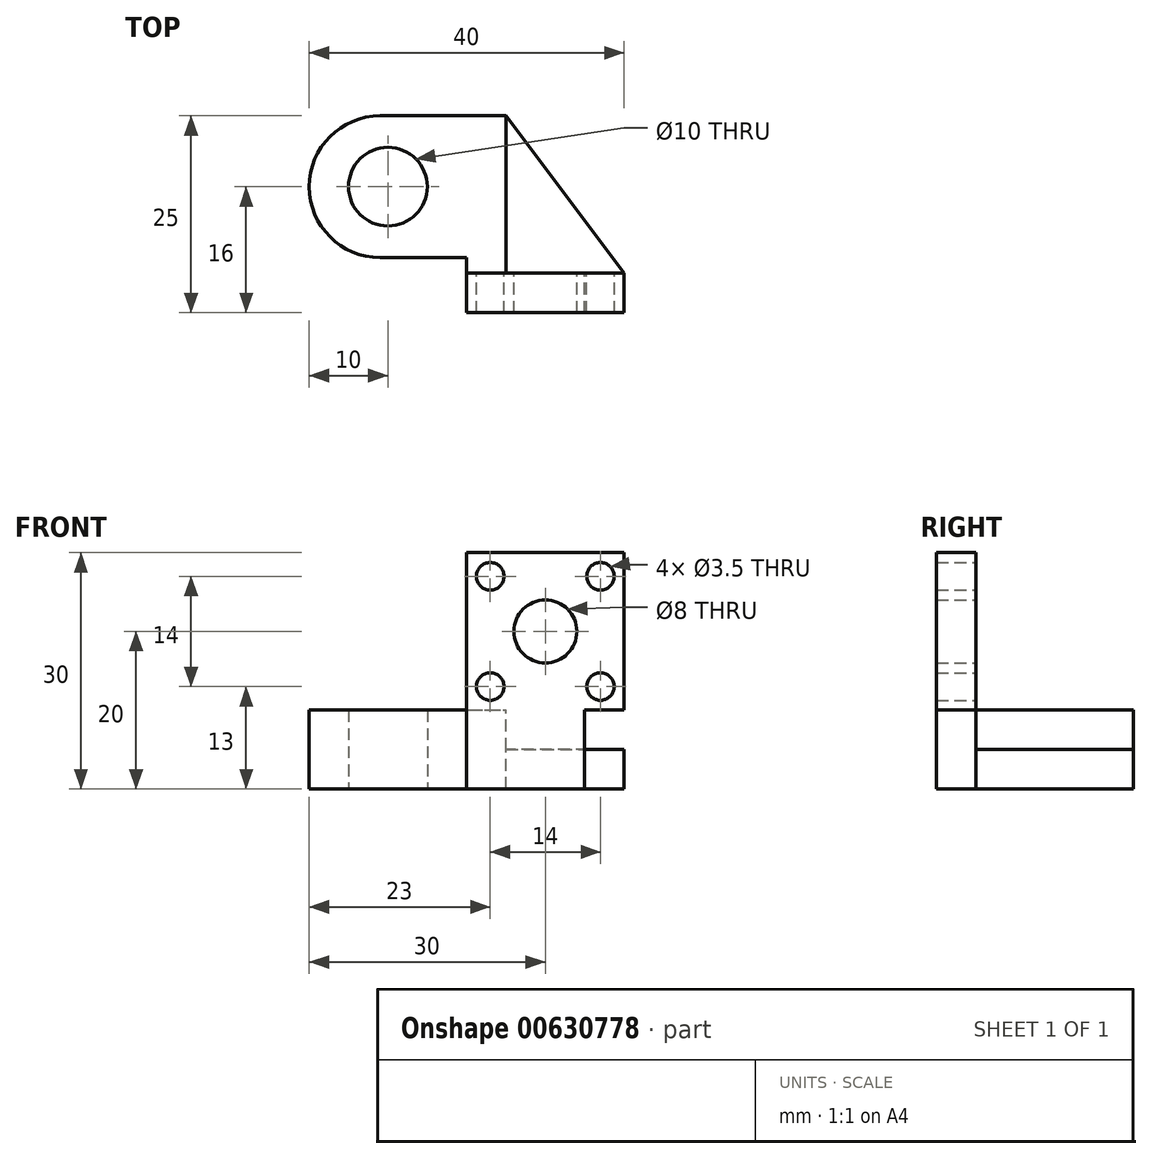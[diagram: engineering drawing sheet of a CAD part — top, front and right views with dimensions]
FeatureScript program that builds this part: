
annotation { "Feature Type Name" : "Feature", "Feature Type Description" : "" }
export const myFeature = defineFeature(function(context is Context, id is Id, definition is map)
    precondition{}
    {
        {
            var Q0;
            Q0=qCreatedBy(makeId("Front.planeOp"),FACE);
            var sketch = newSketch(context, id + "F0", { "sketchPlane" : qUnion([Q0])});
            skCircle(sketch, "E0", {"center": v(0, 0) * mm, "radius": 4 * mm});
            skLineSegment(sketch, "E1.bottom", {"start": v(10, 10) * mm, "end": v(-10, 10) * mm});
            skLineSegment(sketch, "E1.top", {"start": v(10, -20) * mm, "end": v(-10, -20) * mm});
            skLineSegment(sketch, "E1.left", {"start": v(10, 10) * mm, "end": v(10, -20) * mm});
            skLineSegment(sketch, "E1.right", {"start": v(-10, 10) * mm, "end": v(-10, -20) * mm});
            skCircle(sketch, "E2", {"center": v(-7, 7) * mm, "radius": 1.75 * mm});
            skCircle(sketch, "E3", {"center": v(7, 7) * mm, "radius": 1.75 * mm});
            skCircle(sketch, "E4", {"center": v(7, -7) * mm, "radius": 1.75 * mm});
            skCircle(sketch, "E5", {"center": v(-7, -7) * mm, "radius": 1.75 * mm});
            skLineSegment(sketch, "E6.bottom", {"start": v(10, -20) * mm, "end": v(5, -20) * mm});
            skLineSegment(sketch, "E6.top", {"start": v(10, -10) * mm, "end": v(5, -10) * mm});
            skLineSegment(sketch, "E6.left", {"start": v(10, -20) * mm, "end": v(10, -10) * mm});
            skLineSegment(sketch, "E6.right", {"start": v(5, -20) * mm, "end": v(5, -10) * mm});
            skLineSegment(sketch, "E7", {"start": v(0, 0) * mm, "end": v(0, 50.8) * mm, "construction": true});
            skLineSegment(sketch, "E8.MirrorCS", {"start": v(-5, -20) * mm, "end": v(-5, -10) * mm});
            skLineSegment(sketch, "E9.MirrorCS", {"start": v(-10, -10) * mm, "end": v(-5, -10) * mm});
            skSolve(sketch);
        }
        {
            var Q0;
            Q0=makeQuery(id+"F0.imprint","IMPRINT",FACE,{"disambiguationData":[TD([[makeQuery(id+"F0.imprint","IMPRINT",EDGE,{"derivedFrom":sQuery(id+"F0.wireOp",EDGE,"E0")}),-1.0]])]});
            var Q1;
            Q1=makeQuery(id+"F0.imprint","IMPRINT",FACE,{"disambiguationData":[TD([[makeQuery(id+"F0.imprint","IMPRINT",EDGE,{"derivedFrom":sQuery(id+"F0.wireOp",EDGE,"E6.bottom")}),-1.0]])]});
            extrude(context, id + "F1", {"entities" : qUnion([Q0, Q1]), "depth" : 5 * mm, "offsetDistance" : 25 * mm});
        }
        {
            var Q0;
            {var subQ3=sQuery(id+"F0.wireOp",EDGE,"E8.MirrorCS");Q0=makeQuery(id+"F0.imprint","IMPRINT",FACE,{"disambiguationData":[TD([[makeQuery(id+"F0.imprint","IMPRINT",EDGE,{"derivedFrom":subQ3}),1.0]])]});}
            extrude(context, id + "F2", {"entities" : qUnion([Q0]), "operationType" : NewBodyOperationType.ADD, "depth" : 5 * mm, "offsetDistance" : 25 * mm, "hasSecondDirection" : true, "secondDirectionOppositeDirection" : true, "secondDirectionDepth" : 20 * mm});
        }
        {
            var Q0;
            Q0=makeQuery(id+"F2.boolean.opBoolean","MERGE",FACE,{"derivedFrom":[makeQuery(id+"F1.opExtrude","SWEPT_FACE",FACE,{"disambiguationData":[OSD([sQuery(id+"F0.wireOp",EDGE,"E1.top")])]}),makeQuery(id+"F2.opExtrude","SWEPT_FACE",FACE,{"disambiguationData":[OSD([sQuery(id+"F0.wireOp",EDGE,"E6.bottom")])]})]});
            var sketch = newSketch(context, id + "F3", { "sketchPlane" : qUnion([Q0])});
            skLineSegment(sketch, "E10", {"start": v(0, 0) * mm, "end": v(0, 36.2) * mm, "construction": true});
            skLineSegment(sketch, "E11.MirrorCS", {"start": v(-10, -20) * mm, "end": v(-10, -2) * mm});
            skLineSegment(sketch, "E12.MirrorCS", {"start": v(-10, -2) * mm, "end": v(-21, -2) * mm});
            skCircle(sketch, "E13.MirrorC", {"center": v(-20, -11) * mm, "radius": 5 * mm});
            skArc(sketch, "E14.MirrorCS", {"start": v(-30, -11) * mm, "mid": v(-27.36, -4.64) * mm, "end": v(-21, -2) * mm});
            skArc(sketch, "E15.MirrorCS", {"start": v(-21, -20) * mm, "mid": v(-27.36, -17.36) * mm, "end": v(-30, -11) * mm});
            skLineSegment(sketch, "E16.MirrorCS", {"start": v(-10, -20) * mm, "end": v(-21, -20) * mm});
            skLineSegment(sketch, "E17.MirrorCS", {"start": v(-20, 8.06) * mm, "end": v(-20, -30.28) * mm, "construction": true});
            skLineSegment(sketch, "E18.MirrorCS", {"start": v(19.44, -11) * mm, "end": v(-30, -11) * mm, "construction": true});
            skSolve(sketch);
        }
        {
            var Q0;
            Q0=makeQuery(id+"F3.imprint","IMPRINT",FACE,{"disambiguationData":[TD([[makeQuery(id+"F3.imprint","IMPRINT",EDGE,{"derivedFrom":sQuery(id+"F3.wireOp",EDGE,"E11.MirrorCS")}),-1.0]])]});
            extrude(context, id + "F4", {"entities" : qUnion([Q0]), "operationType" : NewBodyOperationType.ADD, "oppositeDirection" : true, "depth" : 10 * mm, "offsetDistance" : 25 * mm});
        }
        {
            var Q0;
            Q0=makeQuery(id+"F4.boolean.opBoolean","MERGE",FACE,{"derivedFrom":[makeQuery(id+"F2.boolean.opBoolean","MERGE",FACE,{"derivedFrom":[makeQuery(id+"F1.opExtrude","SWEPT_FACE",FACE,{"disambiguationData":[OSD([sQuery(id+"F0.wireOp",EDGE,"E1.top")])]}),makeQuery(id+"F2.opExtrude","SWEPT_FACE",FACE,{"disambiguationData":[OSD([sQuery(id+"F0.wireOp",EDGE,"E6.bottom")])]})]}),makeQuery(id+"F4.opExtrude","CAP_FACE",FACE,{"disambiguationData":[OSD([sQuery(id+"F3.wireOp",EDGE,"ABPhrq3E-RsWc-z5md-EiWi-Qo4oXEG86XOk.bottom"),sQuery(id+"F3.wireOp",EDGE,"ABPhrq3E-RsWc-z5md-EiWi-Qo4oXEG86XOk.top"),sQuery(id+"F3.wireOp",EDGE,"ABPhrq3E-RsWc-z5md-EiWi-Qo4oXEG86XOk.left"),sQuery(id+"F3.wireOp",EDGE,"XPBqMR5t-pk4j-waNs-Rl70-sSKM0ePCXRSr"),sQuery(id+"F3.wireOp",EDGE,"753d2c3b-d90f-4cd3-bb09-2d7a23aacffc.filletArc"),sQuery(id+"F3.wireOp",EDGE,"1a6af256-a69d-40ec-95a1-83ec94e579a9.filletArc")])],"isStart":true})]});
            var sketch = newSketch(context, id + "F5", { "sketchPlane" : qUnion([Q0])});
            skLineSegment(sketch, "E19", {"start": v(-10, 0) * mm, "end": v(10, 0) * mm});
            skLineSegment(sketch, "E20", {"start": v(10, 0) * mm, "end": v(-5, -20) * mm});
            skLineSegment(sketch, "E21", {"start": v(-5, -20) * mm, "end": v(-10, 0) * mm});
            skSolve(sketch);
        }
        {
            var Q0;
            Q0=makeQuery(id+"F5.imprint","IMPRINT",FACE,{"disambiguationData":[TD([[makeQuery(id+"F5.imprint","IMPRINT",EDGE,{"derivedFrom":sQuery(id+"F5.wireOp",EDGE,"E19")}),1.0]])]});
            extrude(context, id + "F6", {"entities" : qUnion([Q0]), "operationType" : NewBodyOperationType.ADD, "oppositeDirection" : true, "depth" : 5 * mm, "offsetDistance" : 25 * mm});
        }
    });
